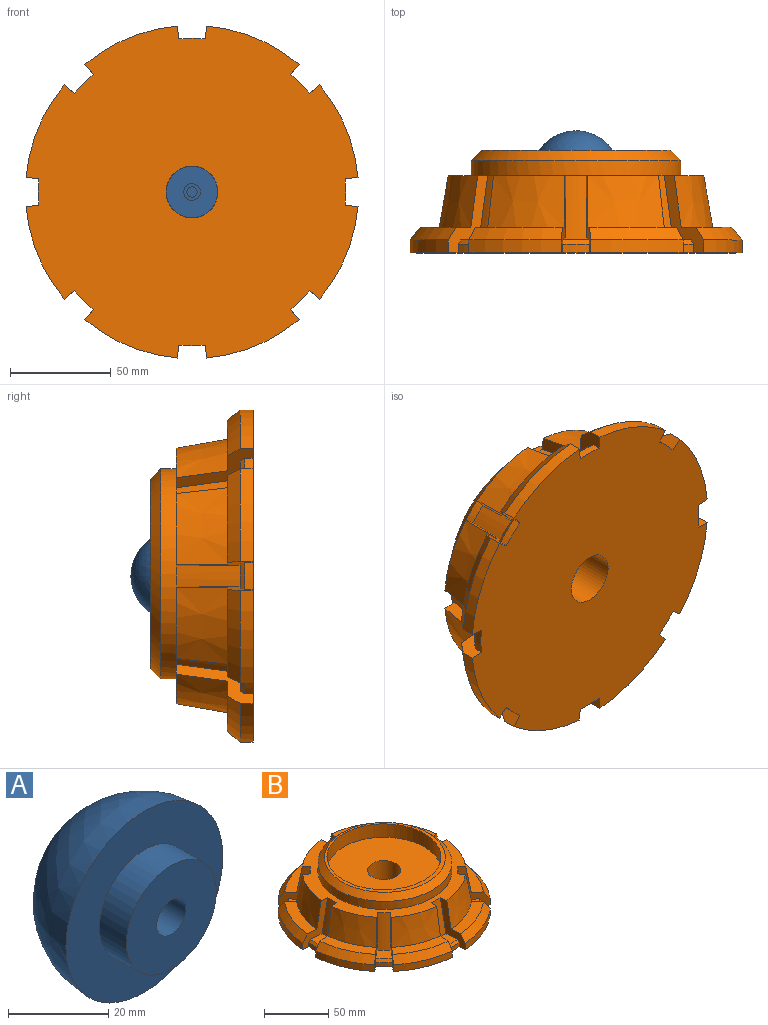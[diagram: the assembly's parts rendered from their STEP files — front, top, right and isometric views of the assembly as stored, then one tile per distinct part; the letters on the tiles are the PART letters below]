
ASSEMBLY  parts=2 mates=1
PART A: 8 faces, bbox 133.1x104.8x133.1 mm
  f0: plane 25.4x25.4mm, normal (0,-1,0), area 453.2mm2, adj f3,f4
  f1: revolved ~44.36x22.18mm, area 0mm2, adj f2
  f2: plane 133.07x133.07mm, normal (0,-1,0), area 1038.7mm2, adj f1,f3
  f3: cylinder r=12.7mm len=25.4mm, axis (0,1,0), area 608mm2, adj f0,f2
  f4: cylinder r=4.13mm len=8.26mm, axis (0,-1,0), area 197.6mm2, adj f0,f5
  f5: plane 8.26x8.26mm, normal (0,-1,0), area 33.3mm2, adj f4,f7
  f6: plane 5.08x5.08mm, normal (0,-1,0), area 20.3mm2, adj f7
  f7: cylinder r=2.54mm len=8.48mm, axis (0,-1,0), area 135.4mm2, adj f5,f6
PART B: 88 faces, bbox 164.4x164.4x50.8 mm
  f0: cone r=63.5mm half-angle=10deg, axis (0,0,-1), area 1035.7mm2, adj f1,f31,f39,f80
  f1: plane 43.84x25.05mm, normal (0,0,1), area 419.4mm2, adj f0,f3,f39,f80
  f2: plane 164.38x164.38mm, normal (0,0,-1), area 20162mm2, adj f4,f8,f12,f16,f20,f24,f28,f33
  f3: cone r=77.42mm half-angle=38.7deg, axis (0,0,-1), area 397.2mm2, adj f1,f4,f39,f80
  f4: cylinder r=82.5mm len=45.84mm, axis (0,0,-1), area 320mm2, adj f2,f3,f39,f80
  f5: cone r=63.5mm half-angle=10deg, axis (0,0,-1), area 1035.7mm2, adj f6,f31,f74,f81
  f6: plane 43.84x25.05mm, normal (0,0,1), area 419.4mm2, adj f5,f7,f74,f81
  f7: cone r=77.42mm half-angle=38.7deg, axis (0,0,-1), area 397.2mm2, adj f6,f8,f74,f81
  f8: cylinder r=82.5mm len=45.84mm, axis (0,0,-1), area 320mm2, adj f2,f7,f74,f81
  f9: cone r=63.5mm half-angle=10deg, axis (0,0,-1), area 1035.7mm2, adj f10,f31,f68,f75
  f10: plane 43.84x25.05mm, normal (0,0,1), area 419.4mm2, adj f9,f11,f68,f75
  f11: cone r=77.42mm half-angle=38.7deg, axis (0,0,-1), area 397.2mm2, adj f10,f12,f68,f75
  f12: cylinder r=82.5mm len=45.84mm, axis (0,0,-1), area 320mm2, adj f2,f11,f68,f75
  f13: cone r=63.5mm half-angle=10deg, axis (0,0,-1), area 1035.7mm2, adj f14,f31,f62,f69
  f14: plane 43.84x25.05mm, normal (0,0,1), area 419.4mm2, adj f13,f15,f62,f69
  f15: cone r=77.42mm half-angle=38.7deg, axis (0,0,-1), area 397.2mm2, adj f14,f16,f62,f69
  f16: cylinder r=82.5mm len=45.84mm, axis (0,0,-1), area 320mm2, adj f2,f15,f62,f69
  f17: cone r=63.5mm half-angle=10deg, axis (0,0,-1), area 1035.7mm2, adj f18,f31,f56,f63
  f18: plane 43.84x25.05mm, normal (0,0,1), area 419.4mm2, adj f17,f19,f56,f63
  f19: cone r=77.42mm half-angle=38.7deg, axis (0,0,-1), area 397.2mm2, adj f18,f20,f56,f63
  f20: cylinder r=82.5mm len=45.84mm, axis (0,0,-1), area 320mm2, adj f2,f19,f56,f63
  f21: cone r=63.5mm half-angle=10deg, axis (0,0,-1), area 1035.7mm2, adj f22,f31,f50,f57
  f22: plane 43.84x25.05mm, normal (0,0,1), area 419.4mm2, adj f21,f23,f50,f57
  f23: cone r=77.42mm half-angle=38.7deg, axis (0,0,-1), area 397.2mm2, adj f22,f24,f50,f57
  f24: cylinder r=82.5mm len=45.84mm, axis (0,0,-1), area 320mm2, adj f2,f23,f50,f57
  f25: cone r=63.5mm half-angle=10deg, axis (0,0,-1), area 1035.7mm2, adj f26,f31,f44,f51
  f26: plane 43.84x25.05mm, normal (0,0,1), area 419.4mm2, adj f25,f27,f44,f51
  f27: cone r=77.42mm half-angle=38.7deg, axis (0,0,-1), area 397.2mm2, adj f26,f28,f44,f51
  f28: cylinder r=82.5mm len=45.84mm, axis (0,0,-1), area 320mm2, adj f2,f27,f44,f51
  f29: cone r=63.5mm half-angle=10deg, axis (0,0,-1), area 1035.7mm2, adj f30,f31,f38,f45
  f30: plane 43.84x25.05mm, normal (0,0,1), area 419.4mm2, adj f29,f32,f38,f45
  f31: plane 126.52x126.52mm, normal (0,0,1), area 3637.8mm2, adj f0,f5,f9,f13,f17,f21,f25,f29
  f32: cone r=77.42mm half-angle=38.7deg, axis (0,0,-1), area 397.2mm2, adj f30,f33,f38,f45
  f33: cylinder r=82.5mm len=45.84mm, axis (0,0,-1), area 320mm2, adj f2,f32,f38,f45
  f34: cone r=57.05mm half-angle=10deg, axis (0,0,-1), area 336.8mm2, adj f31,f37,f38,f39
  f35: cylinder r=76.15mm len=13.27mm, axis (0,0,1), area 54.8mm2, adj f2,f36,f38,f39
  f36: cone r=74.37mm half-angle=38.7deg, axis (0,0,-1), area 37.5mm2, adj f35,f37,f38,f39
  f37: plane 12.96x11.96mm, normal (0,0,1), area 140.2mm2, adj f34,f36,f38,f39
  f38: plane 38.1x25.35mm, normal (-0.09,-1,0), area 319.6mm2, adj f2,f29,f30,f31,f32,f33,f34,f35
  f39: plane 38.1x25.35mm, normal (-0.09,1,0), area 319.6mm2, adj f0,f1,f2,f3,f4,f31,f34,f35
  f40: cone r=57.05mm half-angle=10deg, axis (0,0,-1), area 336.8mm2, adj f31,f43,f44,f45
  f41: cylinder r=76.15mm len=9.39mm, axis (0,0,1), area 54.8mm2, adj f2,f42,f44,f45
  f42: cone r=74.37mm half-angle=38.7deg, axis (0,0,-1), area 37.5mm2, adj f41,f43,f44,f45
  f43: plane 16.7x16.7mm, normal (0,0,1), area 140.2mm2, adj f40,f42,f44,f45
  f44: plane 38.1x19.5mm, normal (-0.77,-0.64,0), area 319.6mm2, adj f2,f25,f26,f27,f28,f31,f40,f41
  f45: plane 38.1x19.5mm, normal (0.64,0.77,0), area 319.6mm2, adj f2,f29,f30,f31,f32,f33,f40,f41
  f46: cone r=57.05mm half-angle=10deg, axis (0,0,-1), area 336.8mm2, adj f31,f49,f50,f51
  f47: cylinder r=76.15mm len=13.27mm, axis (0,0,1), area 54.8mm2, adj f2,f48,f50,f51
  f48: cone r=74.37mm half-angle=38.7deg, axis (0,0,-1), area 37.5mm2, adj f47,f49,f50,f51
  f49: plane 12.96x11.96mm, normal (0,0,1), area 140.2mm2, adj f46,f48,f50,f51
  f50: plane 38.1x25.35mm, normal (-1,0.09,0), area 319.6mm2, adj f2,f21,f22,f23,f24,f31,f46,f47
  f51: plane 38.1x25.35mm, normal (1,0.09,0), area 319.6mm2, adj f2,f25,f26,f27,f28,f31,f46,f47
  f52: cone r=57.05mm half-angle=10deg, axis (0,0,-1), area 336.8mm2, adj f31,f55,f56,f57
  f53: cylinder r=76.15mm len=9.39mm, axis (0,0,1), area 54.8mm2, adj f2,f54,f56,f57
  f54: cone r=74.37mm half-angle=38.7deg, axis (0,0,-1), area 37.5mm2, adj f53,f55,f56,f57
  f55: plane 16.7x16.7mm, normal (0,0,1), area 140.2mm2, adj f52,f54,f56,f57
  f56: plane 38.1x19.5mm, normal (-0.64,0.77,0), area 319.6mm2, adj f2,f17,f18,f19,f20,f31,f52,f53
  f57: plane 38.1x19.5mm, normal (0.77,-0.64,0), area 319.6mm2, adj f2,f21,f22,f23,f24,f31,f52,f53
  f58: cone r=57.05mm half-angle=10deg, axis (0,0,-1), area 336.8mm2, adj f31,f61,f62,f63
  f59: cylinder r=76.15mm len=13.27mm, axis (0,0,1), area 54.8mm2, adj f2,f60,f62,f63
  f60: cone r=74.37mm half-angle=38.7deg, axis (0,0,-1), area 37.5mm2, adj f59,f61,f62,f63
  f61: plane 12.96x11.96mm, normal (0,0,1), area 140.2mm2, adj f58,f60,f62,f63
  f62: plane 38.1x25.35mm, normal (0.09,1,0), area 319.6mm2, adj f2,f13,f14,f15,f16,f31,f58,f59
  f63: plane 38.1x25.35mm, normal (0.09,-1,0), area 319.6mm2, adj f2,f17,f18,f19,f20,f31,f58,f59
  f64: cone r=57.05mm half-angle=10deg, axis (0,0,-1), area 336.8mm2, adj f31,f67,f68,f69
  f65: cylinder r=76.15mm len=9.39mm, axis (0,0,1), area 54.8mm2, adj f2,f66,f68,f69
  f66: cone r=74.37mm half-angle=38.7deg, axis (0,0,-1), area 37.5mm2, adj f65,f67,f68,f69
  f67: plane 16.7x16.7mm, normal (0,0,1), area 140.2mm2, adj f64,f66,f68,f69
  f68: plane 38.1x19.5mm, normal (0.77,0.64,0), area 319.6mm2, adj f2,f9,f10,f11,f12,f31,f64,f65
  f69: plane 38.1x19.5mm, normal (-0.64,-0.77,0), area 319.6mm2, adj f2,f13,f14,f15,f16,f31,f64,f65
  f70: cone r=57.05mm half-angle=10deg, axis (0,0,-1), area 336.8mm2, adj f31,f73,f74,f75
  f71: cylinder r=76.15mm len=13.27mm, axis (0,0,1), area 54.8mm2, adj f2,f72,f74,f75
  f72: cone r=74.37mm half-angle=38.7deg, axis (0,0,-1), area 37.5mm2, adj f71,f73,f74,f75
  f73: plane 12.96x11.96mm, normal (0,0,1), area 140.2mm2, adj f70,f72,f74,f75
  f74: plane 38.1x25.35mm, normal (1,-0.09,0), area 319.6mm2, adj f2,f5,f6,f7,f8,f31,f70,f71
  f75: plane 38.1x25.35mm, normal (-1,-0.09,0), area 319.6mm2, adj f2,f9,f10,f11,f12,f31,f70,f71
  f76: cone r=57.05mm half-angle=10deg, axis (0,0,-1), area 336.8mm2, adj f31,f79,f80,f81
  f77: cylinder r=76.15mm len=9.39mm, axis (0,0,1), area 54.8mm2, adj f2,f78,f80,f81
  f78: cone r=74.37mm half-angle=38.7deg, axis (0,0,-1), area 37.5mm2, adj f77,f79,f80,f81
  f79: plane 16.7x16.7mm, normal (0,0,1), area 140.2mm2, adj f76,f78,f80,f81
  f80: plane 38.1x19.5mm, normal (0.64,-0.77,0), area 319.6mm2, adj f0,f1,f2,f3,f4,f31,f76,f77
  f81: plane 38.1x19.5mm, normal (-0.77,0.64,0), area 319.6mm2, adj f2,f5,f6,f7,f8,f31,f76,f77
  f82: cylinder r=44.22mm len=88.45mm, axis (0,0,-1), area 3528.8mm2, adj f84,f85
  f83: cylinder r=51.98mm len=103.95mm, axis (0,0,-1), area 2488.5mm2, adj f31,f86
  f84: plane 93.79x93.79mm, normal (0,0,1), area 765.4mm2, adj f82,f86
  f85: plane 88.45x88.45mm, normal (0,0,1), area 5624.9mm2, adj f82,f87
  f86: cone r=46.9mm half-angle=45deg, axis (0,0,-1), area 2231.6mm2, adj f83,f84
  f87: cylinder r=12.85mm len=38.1mm, axis (0,0,-1), area 3076.7mm2, adj f2,f85
PLACE A t=(109.72,64.53,15.11)mm
PLACE B rot(axis=(-1,0,0),90deg) t=(109.72,34.05,15.11)mm
MATE parallel A.f3 <-> B.f82  axis (0,-1,0) through (109.72,72.15,15.11)mm
